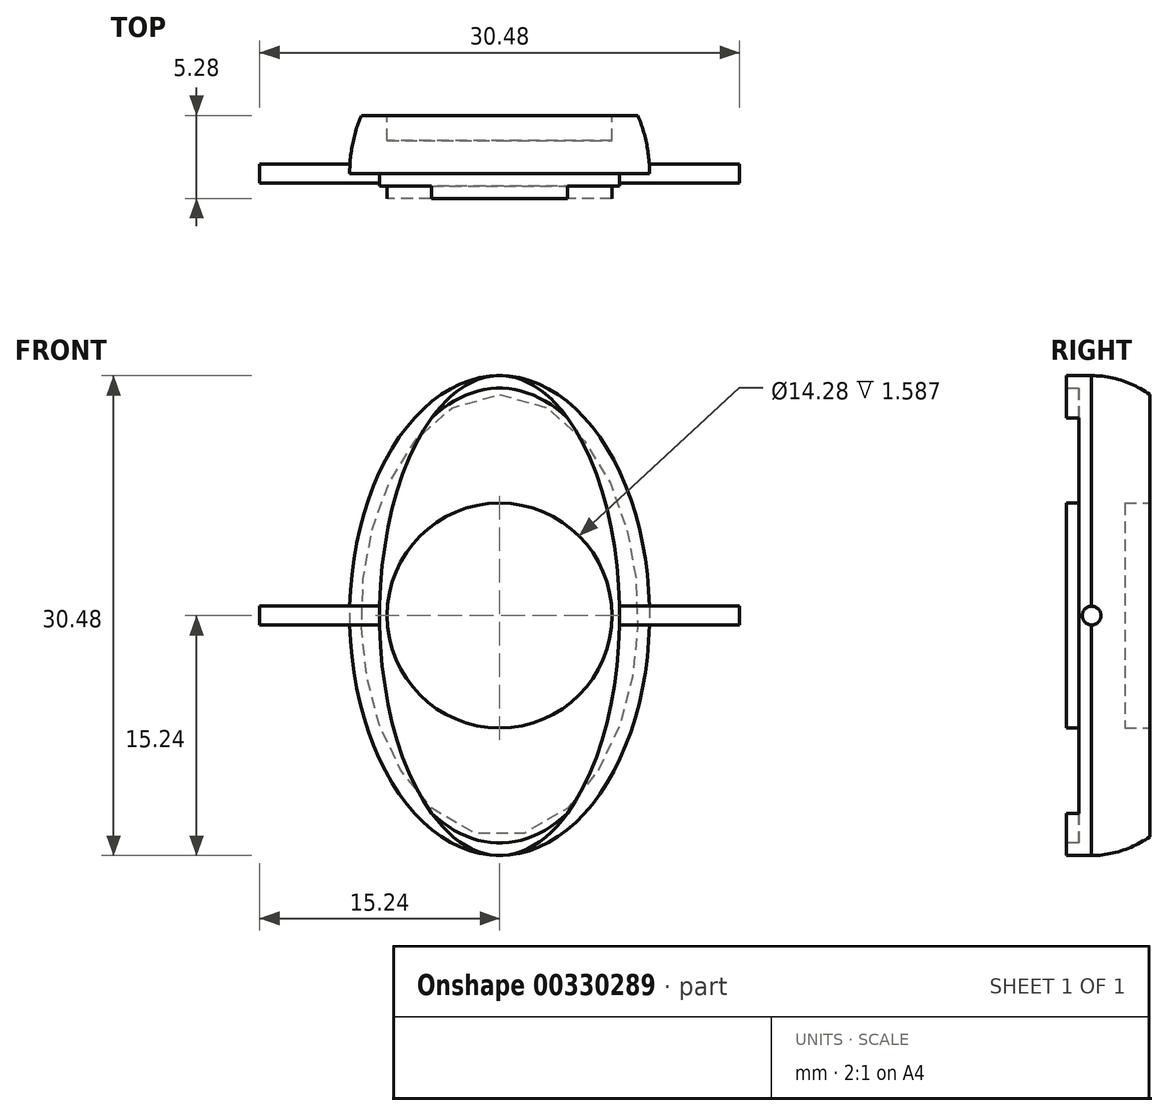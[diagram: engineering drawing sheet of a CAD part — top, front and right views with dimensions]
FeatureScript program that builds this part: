
annotation { "Feature Type Name" : "Feature", "Feature Type Description" : "" }
export const myFeature = defineFeature(function(context is Context, id is Id, definition is map)
    precondition{}
    {
        {
            var Q0;
            Q0=qCreatedBy(makeId("Front.planeOp"),FACE);
            var sketch = newSketch(context, id + "F0", { "sketchPlane" : qUnion([Q0])});
            skEllipticalArc(sketch, "E0", {});
            skLineSegment(sketch, "E1", {"start": v(0, 15.24) * mm, "end": v(0, -15.24) * mm});
            const initialGuessF0  = {"E0": [0, 0, 0, 1, 0.01524, 0.009525, 3.141592653589793, 0]};
            skSetInitialGuess(sketch, initialGuessF0);
            skSolve(sketch);
        }
        {
            var Q0;
            Q0=qSketchRegion(id+"F0",true);
            var Q1;
            Q1=sQuery(id+"F0.wireOp",EDGE,"E1");
            revolve(context, id + "F1", {"entities" : qUnion([Q0]), "axis" : qUnion([Q1]), "revolveType" : RevolveType.ONE_DIRECTION, "oppositeDirection" : true, "angle" : 180 * degree});
        }
        {
            var Q0;
            Q0=qCreatedBy(makeId("Right.planeOp"),FACE);
            var sketch = newSketch(context, id + "F2", { "sketchPlane" : qUnion([Q0])});
            skLineSegment(sketch, "E2.bottom", {"start": v(3.69, 15.9) * mm, "end": v(30.72, 15.9) * mm});
            skLineSegment(sketch, "E2.top", {"start": v(3.69, -22.6) * mm, "end": v(30.72, -22.6) * mm});
            skLineSegment(sketch, "E2.left", {"start": v(3.69, 15.9) * mm, "end": v(3.69, -22.6) * mm});
            skLineSegment(sketch, "E2.right", {"start": v(30.72, 15.9) * mm, "end": v(30.72, -22.6) * mm});
            skSolve(sketch);
        }
        {
            var Q0;
            Q0=qSketchRegion(id+"F2",true);
            extrude(context, id + "F3", {"entities" : qUnion([Q0]), "operationType" : NewBodyOperationType.REMOVE, "oppositeDirection" : true, "depth" : 25.4 * mm, "symmetric" : true});
        }
        {
            var Q0;
            Q0=qCreatedBy(makeId("Right.planeOp"),FACE);
            var sketch = newSketch(context, id + "F4", { "sketchPlane" : qUnion([Q0])});
            skCircle(sketch, "E3", {"center": v(0, 0) * mm, "radius": 0.6 * mm});
            skSolve(sketch);
        }
        {
            var Q0;
            Q0=makeQuery(id+"F1.opRevolve","CAP_FACE",FACE,{"disambiguationData":[OSD([sQuery(id+"F0.wireOp",EDGE,"E0"),sQuery(id+"F0.wireOp",EDGE,"E1")])],"isStart":false});
            var sketch = newSketch(context, id + "F5", { "sketchPlane" : qUnion([Q0])});
            skEllipticalArc(sketch, "E4.0", {});
            skEllipticalArc(sketch, "E4.1", {});
            const initialGuessF5  = {"E4.0": [0, 0, 0, 1, 0.01524, 0.00762, 0, 3.141592653589793], "E4.1": [0, 0, 0, 1, 0.01524, 0.00762, 3.141592653589793, 0]};
            skSetInitialGuess(sketch, initialGuessF5);
            skSolve(sketch);
        }
        {
            var Q0;
            Q0=qSketchRegion(id+"F5",true);
            extrude(context, id + "F6", {"entities" : qUnion([Q0]), "operationType" : NewBodyOperationType.ADD, "depth" : 1.59 * mm});
        }
        {
            var Q0;
            Q0=qSketchRegion(id+"F4",true);
            extrude(context, id + "F7", {"entities" : qUnion([Q0]), "operationType" : NewBodyOperationType.ADD, "depth" : 30.48 * mm, "symmetric" : true});
        }
        {
            var Q0;
            Q0=makeQuery(id+"F6.opExtrude","CAP_FACE",FACE,{"disambiguationData":[OSD([sQuery(id+"F5.wireOp",EDGE,"E4.0"),sQuery(id+"F5.wireOp",EDGE,"E4.1")])],"isStart":false});
            var sketch = newSketch(context, id + "F8", { "sketchPlane" : qUnion([Q0])});
            skEllipse(sketch, "E5", {"center": v(0, 0) * mm, "majorRadius": 14.45 * mm, "minorRadius": 8.73 * mm, "majorAxis": v(0, 1)});
            skSolve(sketch);
        }
        {
            var Q0;
            Q0=qSketchRegion(id+"F8",true);
            extrude(context, id + "F9", {"entities" : qUnion([Q0]), "operationType" : NewBodyOperationType.REMOVE, "oppositeDirection" : true, "depth" : 0.8 * mm});
        }
        {
            var Q0;
            Q0=makeQuery(id+"F9.boolean.opBoolean","COPY",FACE,{"derivedFrom":makeQuery(id+"F9.opExtrude","CAP_FACE",FACE,{"disambiguationData":[OSD([sQuery(id+"F8.wireOp",EDGE,"E5")])],"isStart":false})});
            var sketch = newSketch(context, id + "F10", { "sketchPlane" : qUnion([Q0])});
            skSolve(sketch);
        }
        {
            var Q0;
            Q0=makeQuery(id+"F10.imprint","IMPRINT",FACE,{"disambiguationData":[TD([[makeQuery(id+"F10.imprint","IMPRINT",EDGE,{"derivedFrom":makeQuery(id+"F9.boolean.opBoolean","COPY",EDGE,{"derivedFrom":makeQuery(id+"F9.opExtrude","CAP_EDGE",EDGE,{"disambiguationData":[OSD([sQuery(id+"F8.wireOp",EDGE,"E5")])],"isStart":false})})}),1.0]])]});
            var sketch = newSketch(context, id + "F11", { "sketchPlane" : qUnion([Q0])});
            skCircle(sketch, "E6", {"center": v(0, 0) * mm, "radius": 7.14 * mm});
            skSolve(sketch);
        }
        {
            var Q0;
            Q0=qSketchRegion(id+"F11",true);
            extrude(context, id + "F12", {"entities" : qUnion([Q0]), "operationType" : NewBodyOperationType.ADD, "depth" : 0.8 * mm});
        }
        {
            var Q0;
            Q0=makeQuery(id+"F3.boolean.opBoolean","COPY",FACE,{"derivedFrom":makeQuery(id+"F3.opExtrude","SWEPT_FACE",FACE,{"disambiguationData":[OSD([sQuery(id+"F2.wireOp",EDGE,"E2.left")])]})});
            var sketch = newSketch(context, id + "F13", { "sketchPlane" : qUnion([Q0])});
            skCircle(sketch, "E7.0", {"center": v(0, 0) * mm, "radius": 7.14 * mm});
            skSolve(sketch);
        }
        {
            var Q0;
            Q0=qSketchRegion(id+"F13",true);
            extrude(context, id + "F14", {"entities" : qUnion([Q0]), "operationType" : NewBodyOperationType.REMOVE, "oppositeDirection" : true, "depth" : 1.59 * mm});
        }
    });
